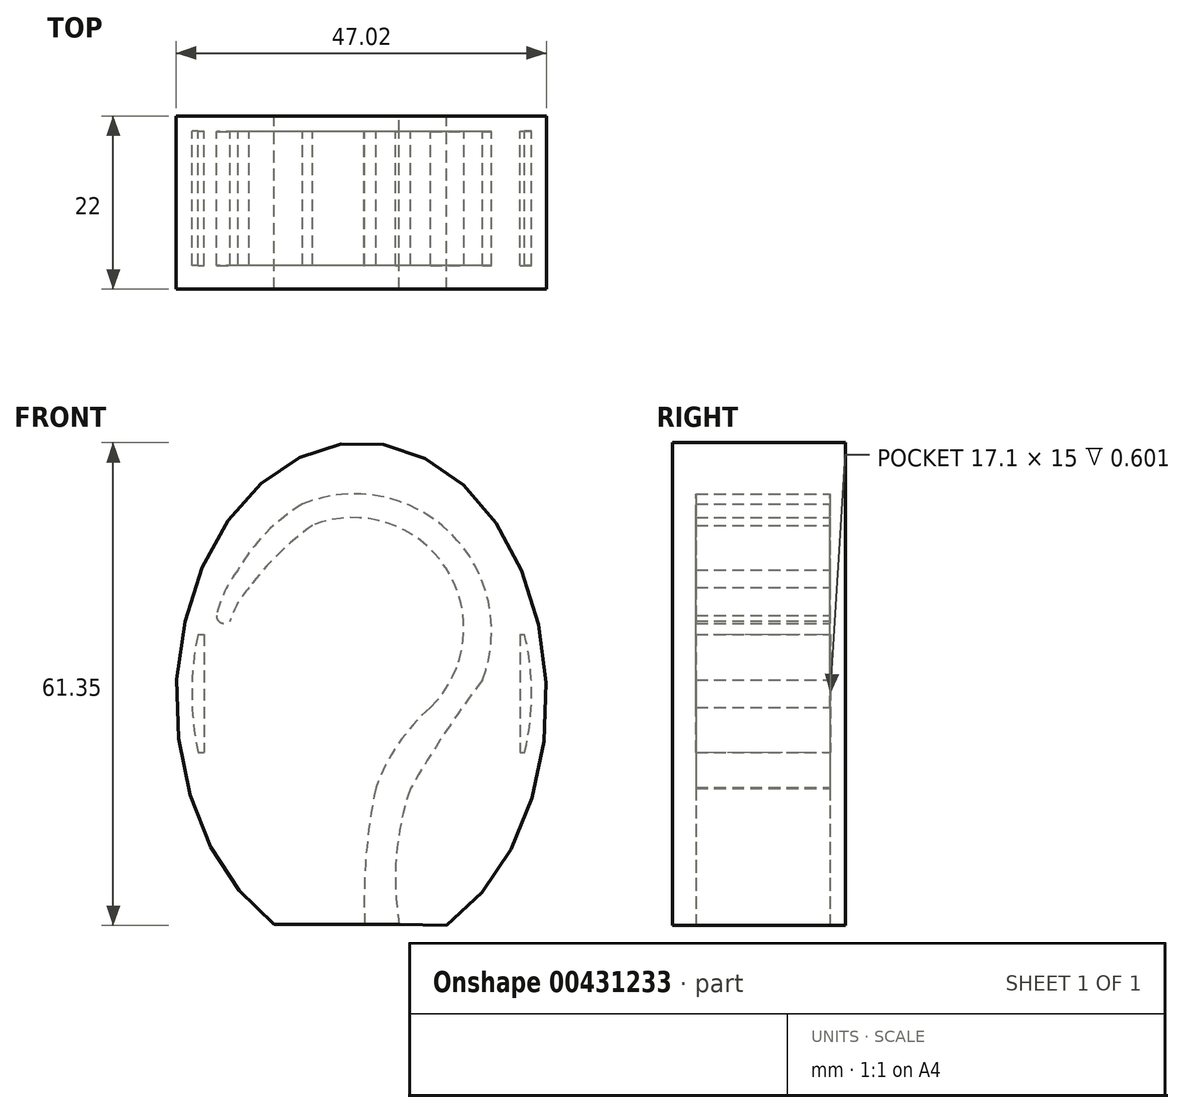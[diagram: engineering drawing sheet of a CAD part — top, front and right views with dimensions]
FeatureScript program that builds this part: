
annotation { "Feature Type Name" : "Feature", "Feature Type Description" : "" }
export const myFeature = defineFeature(function(context is Context, id is Id, definition is map)
    precondition{}
    {
        {
            var Q0;
            Q0=qCreatedBy(makeId("Front.planeOp"),FACE);
            var sketch = newSketch(context, id + "F0", { "sketchPlane" : qUnion([Q0])});
            skArc(sketch, "E0", {"start": v(29.53, -18.8) * mm, "mid": v(31.53, -1.1) * mm, "end": v(14.57, 4.36) * mm});
            skArc(sketch, "E1", {"start": v(14.57, 4.36) * mm, "mid": v(10.23, 0.73) * mm, "end": v(6.52, -3.55) * mm});
            skArc(sketch, "E2", {"start": v(29.53, -18.8) * mm, "mid": v(25.44, -23.44) * mm, "end": v(22.62, -28.96) * mm});
            skArc(sketch, "E3", {"start": v(22.62, -28.96) * mm, "mid": v(21.37, -37.59) * mm, "end": v(21.2, -46.3) * mm});
            skArc(sketch, "E4", {"start": v(36.17, -15.26) * mm, "mid": v(32.05, 3.4) * mm, "end": v(13.3, 7.04) * mm});
            skArc(sketch, "E5", {"start": v(36.17, -15.26) * mm, "mid": v(31.36, -22.04) * mm, "end": v(27, -29.1) * mm});
            skArc(sketch, "E6", {"start": v(27, -29.1) * mm, "mid": v(25.21, -37.61) * mm, "end": v(25.58, -46.3) * mm});
            skArc(sketch, "E7", {"start": v(13.3, 7.04) * mm, "mid": v(8.67, 3.4) * mm, "end": v(5.11, -1.29) * mm});
            skEllipticalArc(sketch, "E8", {});
            skLineSegment(sketch, "E9", {"start": v(31.6, -46.5) * mm, "end": v(25.58, -46.3) * mm});
            skLineSegment(sketch, "E10", {"start": v(21.2, -46.3) * mm, "end": v(9.69, -46.3) * mm});
            skLineSegment(sketch, "E11", {"start": v(21.2, -46.3) * mm, "end": v(25.58, -46.3) * mm});
            skLineSegment(sketch, "E12.bottom", {"start": v(-2, -9.5) * mm, "end": v(0.8, -9.5) * mm});
            skLineSegment(sketch, "E12.top", {"start": v(-2.22, -24.5) * mm, "end": v(0.8, -24.5) * mm});
            skLineSegment(sketch, "E13.trimOffspring", {"start": v(40.9, -24.5) * mm, "end": v(43.75, -24.5) * mm});
            skLineSegment(sketch, "E14.trimOffspring", {"start": v(40.9, -9.5) * mm, "end": v(43.53, -9.5) * mm});
            skArc(sketch, "E15", {"start": v(6.52, -3.55) * mm, "mid": v(5.07, -5.54) * mm, "end": v(4.07, -7.8) * mm});
            skArc(sketch, "E16", {"start": v(5.11, -1.29) * mm, "mid": v(3.43, -4.04) * mm, "end": v(2.36, -7.09) * mm});
            skArc(sketch, "E17", {"start": v(2.36, -7.09) * mm, "mid": v(2.97, -8.03) * mm, "end": v(4.07, -7.8) * mm});
            skLineSegment(sketch, "E18", {"start": v(0.8, -9.5) * mm, "end": v(0.8, -24.5) * mm});
            skLineSegment(sketch, "E19", {"start": v(40.9, -9.5) * mm, "end": v(40.9, -24.5) * mm});
            skPoint(sketch, "E19.endSnap0", {"position": v(41.51, -24.5) * mm});
            skPoint(sketch, "E20.orphan", {"position": v(39.28, -24.5) * mm});
            skArc(sketch, "E21", {"start": v(0, -9.5) * mm, "mid": v(-0.76, -17) * mm, "end": v(0, -24.5) * mm});
            skArc(sketch, "E22", {"start": v(41.51, -24.5) * mm, "mid": v(42.4, -17) * mm, "end": v(41.5, -9.5) * mm});
            const initialGuessF0  = {"E8": [0.020766953006386757, -0.017644768580794334, 0, -1, 0.0325, 0.02351141981592622, 0.4786752717384832, 5.792386282453187]};
            skSetInitialGuess(sketch, initialGuessF0);
            skSolve(sketch);
        }
        {
            var Q0;
            Q0=makeQuery(id+"F0.imprint","IMPRINT",FACE,{"disambiguationData":[TD([[makeQuery(id+"F0.imprint","IMPRINT",EDGE,{"derivedFrom":sQuery(id+"F0.wireOp",EDGE,"E0")}),1.0]])]});
            var Q1;
            Q1=makeQuery(id+"F0.imprint","IMPRINT",FACE,{"disambiguationData":[TD([[makeQuery(id+"F0.imprint","IMPRINT",EDGE,{"derivedFrom":sQuery(id+"F0.wireOp",EDGE,"E0")}),-1.0]])]});
            extrude(context, id + "F1", {"entities" : qUnion([Q0, Q1]), "depth" : 2 * mm});
        }
        {
            var Q0;
            {var subQ0=sQuery(id+"F0.wireOp",EDGE,"ITcKw1nt-J9Ld-67PL-YBSA-eysWHp45b6Hr");Q0=makeQuery(id+"F0.imprint","IMPRINT",FACE,{"disambiguationData":[TD([[makeQuery(id+"F0.imprint","IMPRINT",EDGE,{"derivedFrom":subQ0}),-1.0]])]});}
            var Q1;
            Q1=makeQuery(id+"F0.imprint","IMPRINT",FACE,{"disambiguationData":[TD([[makeQuery(id+"F0.imprint","IMPRINT",EDGE,{"derivedFrom":sQuery(id+"F0.wireOp",EDGE,"E0")}),1.0]])]});
            var Q2;
            {var subQ0=sQuery(id+"F0.wireOp",EDGE,"QHhc20UC-mtx8-icnN-RYlV-OSntLPx70Ntg");Q2=makeQuery(id+"F0.imprint","IMPRINT",FACE,{"disambiguationData":[TD([[makeQuery(id+"F0.imprint","IMPRINT",EDGE,{"derivedFrom":subQ0}),1.0]])]});}
            var Q3;
            {var subQ2=sQuery(id+"F0.wireOp",EDGE,"91twiG9z-I4aJ-VZUw-kTiz-z3GNUcQXl9Px");Q3=makeQuery(id+"F0.imprint","IMPRINT",FACE,{"disambiguationData":[TD([[makeQuery(id+"F0.imprint","IMPRINT",EDGE,{"derivedFrom":subQ2}),1.0]])]});}
            var Q4;
            {var subQ2=sQuery(id+"F0.wireOp",EDGE,"A4A24Ytw-zomU-QQVB-Gdko-3nrFRUeaSvby");Q4=makeQuery(id+"F0.imprint","IMPRINT",FACE,{"disambiguationData":[TD([[makeQuery(id+"F0.imprint","IMPRINT",EDGE,{"derivedFrom":subQ2}),1.0]])]});}
            extrude(context, id + "F2", {"entities" : qUnion([Q0, Q1, Q2, Q3, Q4]), "operationType" : NewBodyOperationType.ADD, "depth" : 19 * mm, "hasSecondDirection" : true, "secondDirectionOppositeDirection" : false, "secondDirectionDepth" : 2 * mm});
        }
        {
            var Q0;
            Q0=makeQuery(id+"F0.imprint","IMPRINT",FACE,{"disambiguationData":[TD([[makeQuery(id+"F0.imprint","IMPRINT",EDGE,{"derivedFrom":sQuery(id+"F0.wireOp",EDGE,"E0")}),1.0]])]});
            var Q1;
            Q1=makeQuery(id+"F0.imprint","IMPRINT",FACE,{"disambiguationData":[TD([[makeQuery(id+"F0.imprint","IMPRINT",EDGE,{"derivedFrom":sQuery(id+"F0.wireOp",EDGE,"E0")}),-1.0]])]});
            var Q2;
            {var subQ0=sQuery(id+"F0.wireOp",EDGE,"ITcKw1nt-J9Ld-67PL-YBSA-eysWHp45b6Hr");Q2=makeQuery(id+"F0.imprint","IMPRINT",FACE,{"disambiguationData":[TD([[makeQuery(id+"F0.imprint","IMPRINT",EDGE,{"derivedFrom":subQ0}),-1.0]])]});}
            var Q3;
            {var subQ5=sQuery(id+"F0.wireOp",EDGE,"A4A24Ytw-zomU-QQVB-Gdko-3nrFRUeaSvby");Q3=makeQuery(id+"F0.imprint","IMPRINT",FACE,{"disambiguationData":[TD([[makeQuery(id+"F0.imprint","IMPRINT",EDGE,{"derivedFrom":subQ5}),-1.0]])]});}
            var Q4;
            {var subQ0=sQuery(id+"F0.wireOp",EDGE,"QHhc20UC-mtx8-icnN-RYlV-OSntLPx70Ntg");Q4=makeQuery(id+"F0.imprint","IMPRINT",FACE,{"disambiguationData":[TD([[makeQuery(id+"F0.imprint","IMPRINT",EDGE,{"derivedFrom":subQ0}),1.0]])]});}
            var Q5;
            {var subQ5=sQuery(id+"F0.wireOp",EDGE,"91twiG9z-I4aJ-VZUw-kTiz-z3GNUcQXl9Px");Q5=makeQuery(id+"F0.imprint","IMPRINT",FACE,{"disambiguationData":[TD([[makeQuery(id+"F0.imprint","IMPRINT",EDGE,{"derivedFrom":subQ5}),-1.0]])]});}
            var Q6;
            {var subQ2=sQuery(id+"F0.wireOp",EDGE,"91twiG9z-I4aJ-VZUw-kTiz-z3GNUcQXl9Px");Q6=makeQuery(id+"F0.imprint","IMPRINT",FACE,{"disambiguationData":[TD([[makeQuery(id+"F0.imprint","IMPRINT",EDGE,{"derivedFrom":subQ2}),1.0]])]});}
            var Q7;
            {var subQ2=sQuery(id+"F0.wireOp",EDGE,"A4A24Ytw-zomU-QQVB-Gdko-3nrFRUeaSvby");Q7=makeQuery(id+"F0.imprint","IMPRINT",FACE,{"disambiguationData":[TD([[makeQuery(id+"F0.imprint","IMPRINT",EDGE,{"derivedFrom":subQ2}),1.0]])]});}
            var Q8;
            {var subQ0=sQuery(id+"F0.wireOp",EDGE,"E19");Q8=makeQuery(id+"F0.imprint","IMPRINT",FACE,{"disambiguationData":[TD([[makeQuery(id+"F0.imprint","IMPRINT",EDGE,{"derivedFrom":subQ0}),1.0]])]});}
            var Q9;
            {var subQ5=sQuery(id+"F0.wireOp",EDGE,"E22");Q9=makeQuery(id+"F0.imprint","IMPRINT",FACE,{"disambiguationData":[TD([[makeQuery(id+"F0.imprint","IMPRINT",EDGE,{"derivedFrom":subQ5}),-1.0]])]});}
            var Q10;
            {var subQ0=sQuery(id+"F0.wireOp",EDGE,"E18");Q10=makeQuery(id+"F0.imprint","IMPRINT",FACE,{"disambiguationData":[TD([[makeQuery(id+"F0.imprint","IMPRINT",EDGE,{"derivedFrom":subQ0}),-1.0]])]});}
            var Q11;
            {var subQ5=sQuery(id+"F0.wireOp",EDGE,"E21");Q11=makeQuery(id+"F0.imprint","IMPRINT",FACE,{"disambiguationData":[TD([[makeQuery(id+"F0.imprint","IMPRINT",EDGE,{"derivedFrom":subQ5}),-1.0]])]});}
            extrude(context, id + "F3", {"entities" : qUnion([Q0, Q1, Q2, Q3, Q4, Q5, Q6, Q7, Q8, Q9, Q10, Q11]), "depth" : 22 * mm, "hasSecondDirection" : true, "secondDirectionOppositeDirection" : false, "secondDirectionDepth" : 19 * mm});
        }
        {
            var Q0;
            {var subQ5=sQuery(id+"F0.wireOp",EDGE,"A4A24Ytw-zomU-QQVB-Gdko-3nrFRUeaSvby");Q0=makeQuery(id+"F0.imprint","IMPRINT",FACE,{"disambiguationData":[TD([[makeQuery(id+"F0.imprint","IMPRINT",EDGE,{"derivedFrom":subQ5}),-1.0]])]});}
            var Q1;
            {var subQ5=sQuery(id+"F0.wireOp",EDGE,"91twiG9z-I4aJ-VZUw-kTiz-z3GNUcQXl9Px");Q1=makeQuery(id+"F0.imprint","IMPRINT",FACE,{"disambiguationData":[TD([[makeQuery(id+"F0.imprint","IMPRINT",EDGE,{"derivedFrom":subQ5}),-1.0]])]});}
            var Q2;
            {var subQ5=sQuery(id+"F0.wireOp",EDGE,"E21");Q2=makeQuery(id+"F0.imprint","IMPRINT",FACE,{"disambiguationData":[TD([[makeQuery(id+"F0.imprint","IMPRINT",EDGE,{"derivedFrom":subQ5}),-1.0]])]});}
            var Q3;
            {var subQ5=sQuery(id+"F0.wireOp",EDGE,"E22");Q3=makeQuery(id+"F0.imprint","IMPRINT",FACE,{"disambiguationData":[TD([[makeQuery(id+"F0.imprint","IMPRINT",EDGE,{"derivedFrom":subQ5}),-1.0]])]});}
            extrude(context, id + "F4", {"entities" : qUnion([Q0, Q1, Q2, Q3]), "operationType" : NewBodyOperationType.ADD, "depth" : 22 * mm});
        }
        {
            var Q0;
            {var subQ0=sQuery(id+"F0.wireOp",EDGE,"ITcKw1nt-J9Ld-67PL-YBSA-eysWHp45b6Hr");Q0=makeQuery(id+"F0.imprint","IMPRINT",FACE,{"disambiguationData":[TD([[makeQuery(id+"F0.imprint","IMPRINT",EDGE,{"derivedFrom":subQ0}),-1.0]])]});}
            var Q1;
            {var subQ2=sQuery(id+"F0.wireOp",EDGE,"A4A24Ytw-zomU-QQVB-Gdko-3nrFRUeaSvby");Q1=makeQuery(id+"F0.imprint","IMPRINT",FACE,{"disambiguationData":[TD([[makeQuery(id+"F0.imprint","IMPRINT",EDGE,{"derivedFrom":subQ2}),1.0]])]});}
            var Q2;
            {var subQ2=sQuery(id+"F0.wireOp",EDGE,"91twiG9z-I4aJ-VZUw-kTiz-z3GNUcQXl9Px");Q2=makeQuery(id+"F0.imprint","IMPRINT",FACE,{"disambiguationData":[TD([[makeQuery(id+"F0.imprint","IMPRINT",EDGE,{"derivedFrom":subQ2}),1.0]])]});}
            var Q3;
            {var subQ0=sQuery(id+"F0.wireOp",EDGE,"E18");Q3=makeQuery(id+"F0.imprint","IMPRINT",FACE,{"disambiguationData":[TD([[makeQuery(id+"F0.imprint","IMPRINT",EDGE,{"derivedFrom":subQ0}),-1.0]])]});}
            var Q4;
            {var subQ0=sQuery(id+"F0.wireOp",EDGE,"E19");Q4=makeQuery(id+"F0.imprint","IMPRINT",FACE,{"disambiguationData":[TD([[makeQuery(id+"F0.imprint","IMPRINT",EDGE,{"derivedFrom":subQ0}),1.0]])]});}
            extrude(context, id + "F5", {"entities" : qUnion([Q0, Q1, Q2, Q3, Q4]), "operationType" : NewBodyOperationType.ADD, "depth" : 1.9 * mm});
        }
    });
